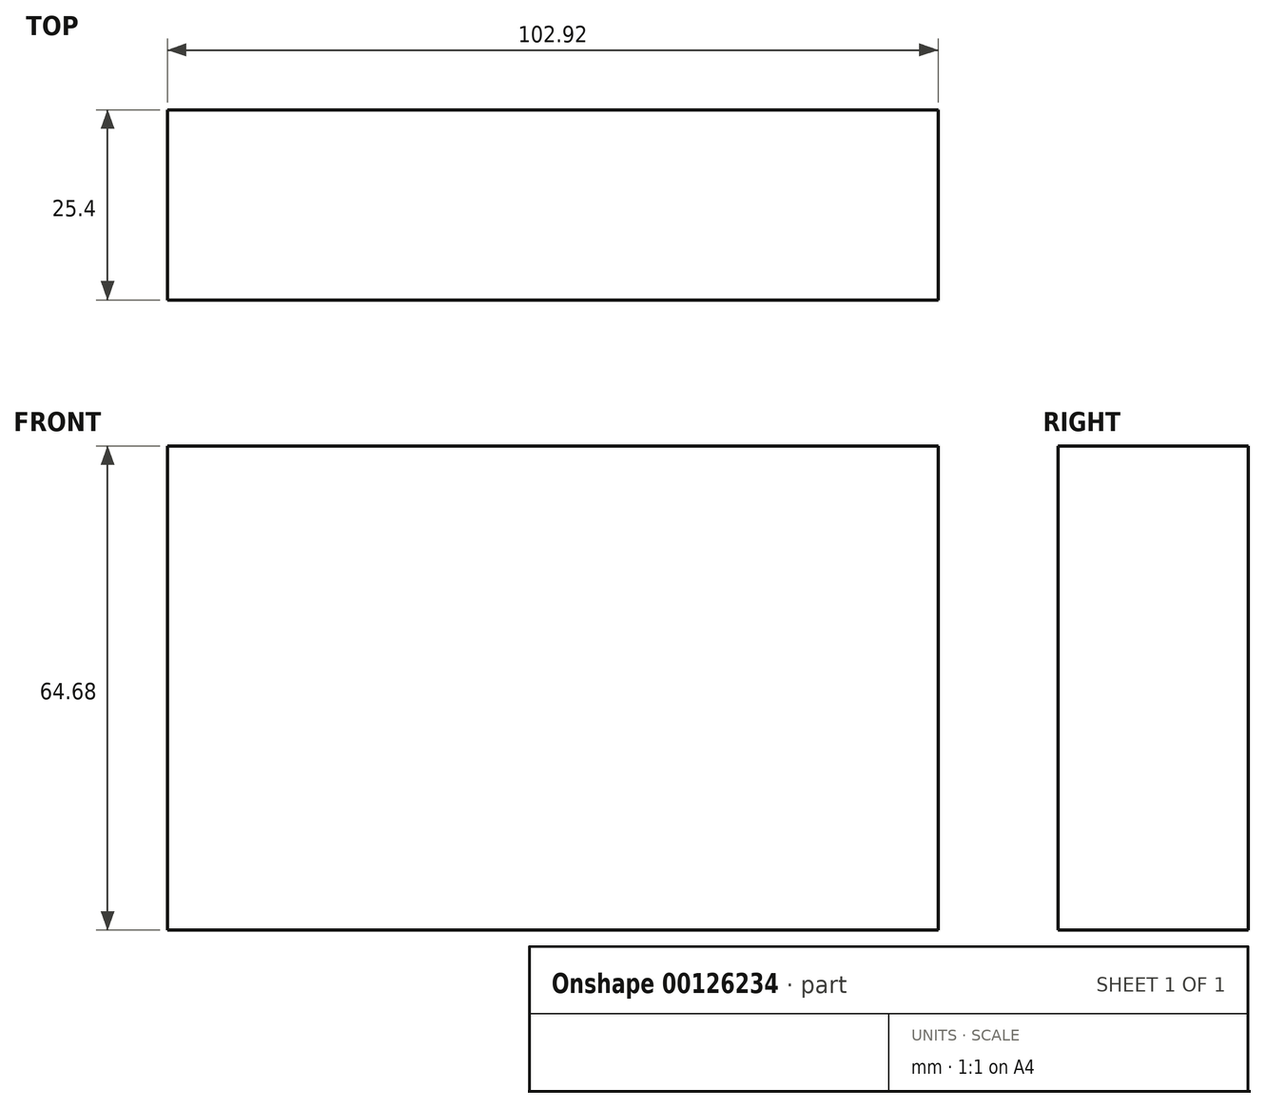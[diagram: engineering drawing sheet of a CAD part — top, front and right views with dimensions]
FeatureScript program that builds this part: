
annotation { "Feature Type Name" : "Feature", "Feature Type Description" : "" }
export const myFeature = defineFeature(function(context is Context, id is Id, definition is map)
    precondition{}
    {
        {
            var Q0;
            Q0=qCreatedBy(makeId("Front.planeOp"),FACE);
            var sketch = newSketch(context, id + "F0", { "sketchPlane" : qUnion([Q0])});
            skLineSegment(sketch, "E0.bottom", {"start": v(51.46, 32.34) * mm, "end": v(-51.46, 32.34) * mm});
            skLineSegment(sketch, "E0.top", {"start": v(51.46, -32.34) * mm, "end": v(-51.46, -32.34) * mm});
            skLineSegment(sketch, "E0.left", {"start": v(51.46, 32.34) * mm, "end": v(51.46, -32.34) * mm});
            skLineSegment(sketch, "E0.right", {"start": v(-51.46, 32.34) * mm, "end": v(-51.46, -32.34) * mm});
            skPoint(sketch, "E0.middle", {"position": v(0, 0) * mm});
            skSolve(sketch);
        }
        {
            var Q0;
            Q0 = qSketchRegion(id + "F0", true);
            extrude(context, id + "F1", {"entities" : qUnion([Q0]), "depth" : 25.4 * mm});
        }
    });
